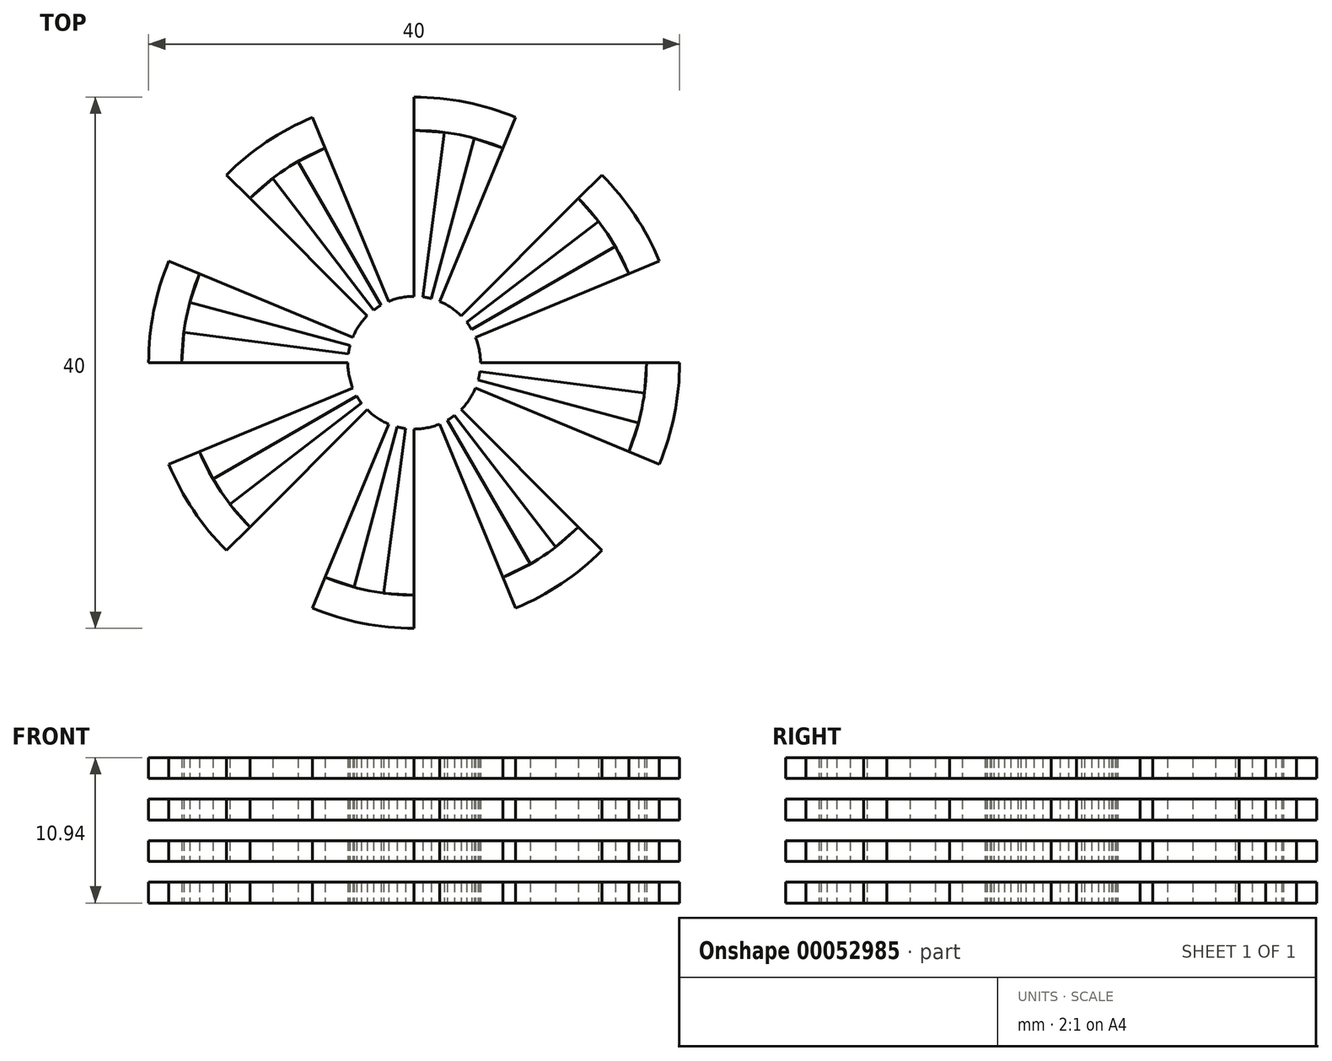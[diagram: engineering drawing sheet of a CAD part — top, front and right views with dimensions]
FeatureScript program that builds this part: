
annotation { "Feature Type Name" : "Feature", "Feature Type Description" : "" }
export const myFeature = defineFeature(function(context is Context, id is Id, definition is map)
    precondition{}
    {
        {
            var Q0;
            Q0=qCreatedBy(makeId("Top.planeOp"),FACE);
            var sketch = newSketch(context, id + "F0", { "sketchPlane" : qUnion([Q0])});
            skCircle(sketch, "E0", {"center": v(0, 0) * mm, "radius": 20 * mm});
            skCircle(sketch, "E1.cCircle", {"center": v(0, 0) * mm, "radius": 20 * mm, "construction": true});
            skLineSegment(sketch, "E1.0", {"start": v(0, -20) * mm, "end": v(-7.65, -18.48) * mm, "construction": true});
            skLineSegment(sketch, "E1.1", {"start": v(-7.65, -18.48) * mm, "end": v(-14.14, -14.14) * mm, "construction": true});
            skLineSegment(sketch, "E1.2", {"start": v(-14.14, -14.14) * mm, "end": v(-18.48, -7.65) * mm, "construction": true});
            skLineSegment(sketch, "E1.3", {"start": v(-18.48, -7.65) * mm, "end": v(-20, 0) * mm, "construction": true});
            skLineSegment(sketch, "E1.4", {"start": v(-20, 0) * mm, "end": v(-18.48, 7.65) * mm, "construction": true});
            skLineSegment(sketch, "E1.5", {"start": v(-18.48, 7.65) * mm, "end": v(-14.14, 14.14) * mm, "construction": true});
            skLineSegment(sketch, "E1.6", {"start": v(-14.14, 14.14) * mm, "end": v(-7.65, 18.48) * mm, "construction": true});
            skLineSegment(sketch, "E1.7", {"start": v(-7.65, 18.48) * mm, "end": v(0, 20) * mm, "construction": true});
            skLineSegment(sketch, "E1.8", {"start": v(0, 20) * mm, "end": v(7.65, 18.48) * mm, "construction": true});
            skLineSegment(sketch, "E1.9", {"start": v(7.65, 18.48) * mm, "end": v(14.14, 14.14) * mm, "construction": true});
            skLineSegment(sketch, "E1.10", {"start": v(14.14, 14.14) * mm, "end": v(18.48, 7.65) * mm, "construction": true});
            skLineSegment(sketch, "E1.11", {"start": v(18.48, 7.65) * mm, "end": v(20, 0) * mm, "construction": true});
            skLineSegment(sketch, "E1.12", {"start": v(20, 0) * mm, "end": v(18.48, -7.65) * mm, "construction": true});
            skLineSegment(sketch, "E1.13", {"start": v(18.48, -7.65) * mm, "end": v(14.14, -14.14) * mm, "construction": true});
            skLineSegment(sketch, "E1.14", {"start": v(14.14, -14.14) * mm, "end": v(7.65, -18.48) * mm, "construction": true});
            skLineSegment(sketch, "E1.15", {"start": v(7.65, -18.48) * mm, "end": v(0, -20) * mm, "construction": true});
            skLineSegment(sketch, "E2", {"start": v(0, 20) * mm, "end": v(0, -20) * mm});
            skLineSegment(sketch, "E3", {"start": v(7.65, -18.48) * mm, "end": v(-7.65, 18.48) * mm});
            skLineSegment(sketch, "E4", {"start": v(14.14, -14.14) * mm, "end": v(-14.14, 14.14) * mm});
            skLineSegment(sketch, "E5", {"start": v(18.48, -7.65) * mm, "end": v(-18.48, 7.65) * mm});
            skLineSegment(sketch, "E6", {"start": v(20, 0) * mm, "end": v(-20, 0) * mm});
            skLineSegment(sketch, "E7", {"start": v(18.48, 7.65) * mm, "end": v(-18.48, -7.65) * mm});
            skLineSegment(sketch, "E8", {"start": v(14.14, 14.14) * mm, "end": v(-14.14, -14.14) * mm});
            skLineSegment(sketch, "E9", {"start": v(7.65, 18.48) * mm, "end": v(-7.65, -18.48) * mm});
            skCircle(sketch, "E10", {"center": v(0, 0) * mm, "radius": 17.5 * mm});
            skSolve(sketch);
        }
        {
            var Q0;
            Q0 = qSketchRegion(id + "F0", true);
            extrude(context, id + "F1", {"entities" : qUnion([Q0]), "depth" : 12.5 * mm});
        }
        {
            var Q0;
            {var subQ0=sQuery(id+"F0.wireOp",EDGE,"E2");var subQ1=sQuery(id+"F0.wireOp",EDGE,"E0");var subQ2=makeQuery(id+"F0.imprint","INTERSECT",VERTEX,{"disambiguationData":[OD(0.0)],"derivedFrom":[subQ1,subQ0]});Q0=makeQuery(id+"F0.imprint","IMPRINT",FACE,{"disambiguationData":[TD([[makeQuery(id+"F0.imprint","IMPRINT",EDGE,{"disambiguationData":[TD([[subQ2,-1.0]])],"derivedFrom":subQ1}),1.0]])]});}
            var Q1;
            {var subQ0=sQuery(id+"F0.wireOp",EDGE,"E4");var subQ1=sQuery(id+"F0.wireOp",EDGE,"E0");var subQ2=makeQuery(id+"F0.imprint","INTERSECT",VERTEX,{"disambiguationData":[OD(1.0)],"derivedFrom":[subQ1,subQ0]});Q1=makeQuery(id+"F0.imprint","IMPRINT",FACE,{"disambiguationData":[TD([[makeQuery(id+"F0.imprint","IMPRINT",EDGE,{"disambiguationData":[TD([[subQ2,-1.0]])],"derivedFrom":subQ1}),1.0]])]});}
            var Q2;
            {var subQ0=sQuery(id+"F0.wireOp",EDGE,"E6");var subQ1=sQuery(id+"F0.wireOp",EDGE,"E0");var subQ2=makeQuery(id+"F0.imprint","INTERSECT",VERTEX,{"disambiguationData":[OD(1.0)],"derivedFrom":[subQ1,subQ0]});Q2=makeQuery(id+"F0.imprint","IMPRINT",FACE,{"disambiguationData":[TD([[makeQuery(id+"F0.imprint","IMPRINT",EDGE,{"disambiguationData":[TD([[subQ2,-1.0]])],"derivedFrom":subQ1}),1.0]])]});}
            var Q3;
            {var subQ0=sQuery(id+"F0.wireOp",EDGE,"E8");var subQ1=sQuery(id+"F0.wireOp",EDGE,"E0");var subQ2=makeQuery(id+"F0.imprint","INTERSECT",VERTEX,{"disambiguationData":[OD(1.0)],"derivedFrom":[subQ1,subQ0]});Q3=makeQuery(id+"F0.imprint","IMPRINT",FACE,{"disambiguationData":[TD([[makeQuery(id+"F0.imprint","IMPRINT",EDGE,{"disambiguationData":[TD([[subQ2,-1.0]])],"derivedFrom":subQ1}),1.0]])]});}
            var Q4;
            {var subQ0=sQuery(id+"F0.wireOp",EDGE,"E2");var subQ1=sQuery(id+"F0.wireOp",EDGE,"E0");var subQ2=makeQuery(id+"F0.imprint","INTERSECT",VERTEX,{"disambiguationData":[OD(1.0)],"derivedFrom":[subQ1,subQ0]});Q4=makeQuery(id+"F0.imprint","IMPRINT",FACE,{"disambiguationData":[TD([[makeQuery(id+"F0.imprint","IMPRINT",EDGE,{"disambiguationData":[TD([[subQ2,-1.0]])],"derivedFrom":subQ1}),1.0]])]});}
            var Q5;
            {var subQ0=sQuery(id+"F0.wireOp",EDGE,"E4");var subQ1=sQuery(id+"F0.wireOp",EDGE,"E0");var subQ2=makeQuery(id+"F0.imprint","INTERSECT",VERTEX,{"disambiguationData":[OD(0.0)],"derivedFrom":[subQ1,subQ0]});Q5=makeQuery(id+"F0.imprint","IMPRINT",FACE,{"disambiguationData":[TD([[makeQuery(id+"F0.imprint","IMPRINT",EDGE,{"disambiguationData":[TD([[subQ2,-1.0]])],"derivedFrom":subQ1}),1.0]])]});}
            var Q6;
            {var subQ0=sQuery(id+"F0.wireOp",EDGE,"E6");var subQ1=sQuery(id+"F0.wireOp",EDGE,"E0");var subQ2=makeQuery(id+"F0.imprint","INTERSECT",VERTEX,{"disambiguationData":[OD(0.0)],"derivedFrom":[subQ1,subQ0]});Q6=makeQuery(id+"F0.imprint","IMPRINT",FACE,{"disambiguationData":[TD([[makeQuery(id+"F0.imprint","IMPRINT",EDGE,{"disambiguationData":[TD([[subQ2,-1.0]])],"derivedFrom":subQ1}),1.0]])]});}
            var Q7;
            {var subQ0=sQuery(id+"F0.wireOp",EDGE,"E8");var subQ1=sQuery(id+"F0.wireOp",EDGE,"E0");var subQ2=makeQuery(id+"F0.imprint","INTERSECT",VERTEX,{"disambiguationData":[OD(0.0)],"derivedFrom":[subQ1,subQ0]});Q7=makeQuery(id+"F0.imprint","IMPRINT",FACE,{"disambiguationData":[TD([[makeQuery(id+"F0.imprint","IMPRINT",EDGE,{"disambiguationData":[TD([[subQ2,-1.0]])],"derivedFrom":subQ1}),1.0]])]});}
            extrude(context, id + "F2", {"entities" : qUnion([Q0, Q1, Q2, Q3, Q4, Q5, Q6, Q7]), "operationType" : NewBodyOperationType.REMOVE, "depth" : 12.5 * mm});
        }
        {
            var Q0;
            Q0=qCreatedBy(makeId("Top.planeOp"),FACE);
            var sketch = newSketch(context, id + "F3", { "sketchPlane" : qUnion([Q0])});
            skCircle(sketch, "E11.cCircle", {"center": v(0, 0) * mm, "radius": 17.5 * mm});
            skLineSegment(sketch, "E11.0", {"start": v(0, 17.5) * mm, "end": v(2.28, 17.35) * mm});
            skLineSegment(sketch, "E11.1", {"start": v(2.28, 17.35) * mm, "end": v(4.53, 16.9) * mm});
            skLineSegment(sketch, "E11.2", {"start": v(4.53, 16.9) * mm, "end": v(6.7, 16.17) * mm});
            skLineSegment(sketch, "E11.3", {"start": v(6.7, 16.17) * mm, "end": v(8.75, 15.16) * mm});
            skLineSegment(sketch, "E11.4", {"start": v(8.75, 15.16) * mm, "end": v(10.65, 13.88) * mm});
            skLineSegment(sketch, "E11.5", {"start": v(10.65, 13.88) * mm, "end": v(12.37, 12.37) * mm});
            skLineSegment(sketch, "E11.6", {"start": v(12.37, 12.37) * mm, "end": v(13.88, 10.65) * mm});
            skLineSegment(sketch, "E11.7", {"start": v(13.88, 10.65) * mm, "end": v(15.16, 8.75) * mm});
            skLineSegment(sketch, "E11.8", {"start": v(15.16, 8.75) * mm, "end": v(16.17, 6.7) * mm});
            skLineSegment(sketch, "E11.9", {"start": v(16.17, 6.7) * mm, "end": v(16.9, 4.53) * mm});
            skLineSegment(sketch, "E11.10", {"start": v(16.9, 4.53) * mm, "end": v(17.35, 2.28) * mm});
            skLineSegment(sketch, "E11.11", {"start": v(17.35, 2.28) * mm, "end": v(17.5, 0) * mm});
            skLineSegment(sketch, "E11.12", {"start": v(17.5, 0) * mm, "end": v(17.35, -2.28) * mm});
            skLineSegment(sketch, "E11.13", {"start": v(17.35, -2.28) * mm, "end": v(16.9, -4.53) * mm});
            skLineSegment(sketch, "E11.14", {"start": v(16.9, -4.53) * mm, "end": v(16.17, -6.7) * mm});
            skLineSegment(sketch, "E11.15", {"start": v(16.17, -6.7) * mm, "end": v(15.16, -8.75) * mm});
            skLineSegment(sketch, "E11.16", {"start": v(15.16, -8.75) * mm, "end": v(13.88, -10.65) * mm});
            skLineSegment(sketch, "E11.17", {"start": v(13.88, -10.65) * mm, "end": v(12.37, -12.37) * mm});
            skLineSegment(sketch, "E11.18", {"start": v(12.37, -12.37) * mm, "end": v(10.65, -13.88) * mm});
            skLineSegment(sketch, "E11.19", {"start": v(10.65, -13.88) * mm, "end": v(8.75, -15.16) * mm});
            skLineSegment(sketch, "E11.20", {"start": v(8.75, -15.16) * mm, "end": v(6.7, -16.17) * mm});
            skLineSegment(sketch, "E11.21", {"start": v(6.7, -16.17) * mm, "end": v(4.53, -16.9) * mm});
            skLineSegment(sketch, "E11.22", {"start": v(4.53, -16.9) * mm, "end": v(2.28, -17.35) * mm});
            skLineSegment(sketch, "E11.23", {"start": v(2.28, -17.35) * mm, "end": v(0, -17.5) * mm});
            skLineSegment(sketch, "E11.24", {"start": v(0, -17.5) * mm, "end": v(-2.28, -17.35) * mm});
            skLineSegment(sketch, "E11.25", {"start": v(-2.28, -17.35) * mm, "end": v(-4.53, -16.9) * mm});
            skLineSegment(sketch, "E11.26", {"start": v(-4.53, -16.9) * mm, "end": v(-6.7, -16.17) * mm});
            skLineSegment(sketch, "E11.27", {"start": v(-6.7, -16.17) * mm, "end": v(-8.75, -15.16) * mm});
            skLineSegment(sketch, "E11.28", {"start": v(-8.75, -15.16) * mm, "end": v(-10.65, -13.88) * mm});
            skLineSegment(sketch, "E11.29", {"start": v(-10.65, -13.88) * mm, "end": v(-12.37, -12.37) * mm});
            skLineSegment(sketch, "E11.30", {"start": v(-12.37, -12.37) * mm, "end": v(-13.88, -10.65) * mm});
            skLineSegment(sketch, "E11.31", {"start": v(-13.88, -10.65) * mm, "end": v(-15.16, -8.75) * mm});
            skLineSegment(sketch, "E11.32", {"start": v(-15.16, -8.75) * mm, "end": v(-16.17, -6.7) * mm});
            skLineSegment(sketch, "E11.33", {"start": v(-16.17, -6.7) * mm, "end": v(-16.9, -4.53) * mm});
            skLineSegment(sketch, "E11.34", {"start": v(-16.9, -4.53) * mm, "end": v(-17.35, -2.28) * mm});
            skLineSegment(sketch, "E11.35", {"start": v(-17.35, -2.28) * mm, "end": v(-17.5, 0) * mm});
            skLineSegment(sketch, "E11.36", {"start": v(-17.5, 0) * mm, "end": v(-17.35, 2.28) * mm});
            skLineSegment(sketch, "E11.37", {"start": v(-17.35, 2.28) * mm, "end": v(-16.9, 4.53) * mm});
            skLineSegment(sketch, "E11.38", {"start": v(-16.9, 4.53) * mm, "end": v(-16.17, 6.7) * mm});
            skLineSegment(sketch, "E11.39", {"start": v(-16.17, 6.7) * mm, "end": v(-15.16, 8.75) * mm});
            skLineSegment(sketch, "E11.40", {"start": v(-15.16, 8.75) * mm, "end": v(-13.88, 10.65) * mm});
            skLineSegment(sketch, "E11.41", {"start": v(-13.88, 10.65) * mm, "end": v(-12.37, 12.37) * mm});
            skLineSegment(sketch, "E11.42", {"start": v(-12.37, 12.37) * mm, "end": v(-10.65, 13.88) * mm});
            skLineSegment(sketch, "E11.43", {"start": v(-10.65, 13.88) * mm, "end": v(-8.75, 15.16) * mm});
            skLineSegment(sketch, "E11.44", {"start": v(-8.75, 15.16) * mm, "end": v(-6.7, 16.17) * mm});
            skLineSegment(sketch, "E11.45", {"start": v(-6.7, 16.17) * mm, "end": v(-4.53, 16.9) * mm});
            skLineSegment(sketch, "E11.46", {"start": v(-4.53, 16.9) * mm, "end": v(-2.28, 17.35) * mm});
            skLineSegment(sketch, "E11.47", {"start": v(-2.28, 17.35) * mm, "end": v(0, 17.5) * mm});
            skLineSegment(sketch, "E12", {"start": v(0, 17.5) * mm, "end": v(0, 0) * mm});
            skLineSegment(sketch, "E13", {"start": v(2.28, 17.35) * mm, "end": v(0, 0) * mm});
            skLineSegment(sketch, "E14", {"start": v(4.53, 16.9) * mm, "end": v(0, 0) * mm});
            skLineSegment(sketch, "E15", {"start": v(6.7, 16.17) * mm, "end": v(0, 0) * mm});
            skLineSegment(sketch, "E16", {"start": v(12.37, 12.37) * mm, "end": v(0, 0) * mm});
            skLineSegment(sketch, "E17", {"start": v(13.88, 10.65) * mm, "end": v(0, 0) * mm});
            skLineSegment(sketch, "E18", {"start": v(15.16, 8.75) * mm, "end": v(0, 0) * mm});
            skLineSegment(sketch, "E19", {"start": v(16.17, 6.7) * mm, "end": v(0, 0) * mm});
            skCircle(sketch, "E20", {"center": v(0, 0) * mm, "radius": 5 * mm});
            skLineSegment(sketch, "E21", {"start": v(17.5, 0) * mm, "end": v(0, 0) * mm});
            skLineSegment(sketch, "E22", {"start": v(17.35, -2.28) * mm, "end": v(0, 0) * mm});
            skLineSegment(sketch, "E23", {"start": v(16.9, -4.53) * mm, "end": v(0, 0) * mm});
            skLineSegment(sketch, "E24", {"start": v(16.17, -6.7) * mm, "end": v(0, 0) * mm});
            skLineSegment(sketch, "E25", {"start": v(12.37, -12.37) * mm, "end": v(0, 0) * mm});
            skLineSegment(sketch, "E26", {"start": v(10.65, -13.88) * mm, "end": v(0, 0) * mm});
            skLineSegment(sketch, "E27", {"start": v(8.75, -15.16) * mm, "end": v(0, 0) * mm});
            skLineSegment(sketch, "E28", {"start": v(6.7, -16.17) * mm, "end": v(0, 0) * mm});
            skLineSegment(sketch, "E29", {"start": v(0, 0) * mm, "end": v(0, -17.5) * mm});
            skLineSegment(sketch, "E30", {"start": v(0, 0) * mm, "end": v(-2.28, -17.35) * mm});
            skLineSegment(sketch, "E31", {"start": v(0, 0) * mm, "end": v(-4.53, -16.9) * mm});
            skLineSegment(sketch, "E32", {"start": v(0, 0) * mm, "end": v(-6.7, -16.17) * mm});
            skLineSegment(sketch, "E33", {"start": v(0, 0) * mm, "end": v(-12.37, -12.37) * mm});
            skLineSegment(sketch, "E34", {"start": v(0, 0) * mm, "end": v(-13.88, -10.65) * mm});
            skLineSegment(sketch, "E35", {"start": v(0, 0) * mm, "end": v(-15.16, -8.75) * mm});
            skLineSegment(sketch, "E36", {"start": v(0, 0) * mm, "end": v(-16.17, -6.7) * mm});
            skLineSegment(sketch, "E37", {"start": v(0, 0) * mm, "end": v(-17.5, 0) * mm});
            skLineSegment(sketch, "E38", {"start": v(0, 0) * mm, "end": v(-17.35, 2.28) * mm});
            skLineSegment(sketch, "E39", {"start": v(0, 0) * mm, "end": v(-16.9, 4.53) * mm});
            skLineSegment(sketch, "E40", {"start": v(0, 0) * mm, "end": v(-16.17, 6.7) * mm});
            skLineSegment(sketch, "E41", {"start": v(0, 0) * mm, "end": v(-12.37, 12.37) * mm});
            skLineSegment(sketch, "E42", {"start": v(0, 0) * mm, "end": v(-10.65, 13.88) * mm});
            skLineSegment(sketch, "E43", {"start": v(0, 0) * mm, "end": v(-8.75, 15.16) * mm});
            skLineSegment(sketch, "E44", {"start": v(0, 0) * mm, "end": v(-6.7, 16.17) * mm});
            skSolve(sketch);
        }
        {
            var Q0;
            {var subQ0=sQuery(id+"F3.wireOp",EDGE,"E31");var subQ1=sQuery(id+"F3.wireOp",EDGE,"E20");var subQ2=makeQuery(id+"F3.imprint","INTERSECT",VERTEX,{"derivedFrom":[subQ1,subQ0]});Q0=makeQuery(id+"F3.imprint","IMPRINT",FACE,{"disambiguationData":[TD([[makeQuery(id+"F3.imprint","IMPRINT",EDGE,{"disambiguationData":[TD([[subQ2,-1.0]])],"derivedFrom":subQ1}),1.0]])]});}
            var Q1;
            {var subQ1=sQuery(id+"F3.wireOp",EDGE,"E17");var subQ3=sQuery(id+"F3.wireOp",EDGE,"E20");var subQ4=makeQuery(id+"F3.imprint","INTERSECT",VERTEX,{"derivedFrom":[subQ1,subQ3]});Q1=makeQuery(id+"F3.imprint","IMPRINT",FACE,{"disambiguationData":[TD([[makeQuery(id+"F3.imprint","IMPRINT",EDGE,{"disambiguationData":[TD([[subQ4,1.0]])],"derivedFrom":subQ3}),1.0]])]});}
            var Q2;
            {var subQ0=sQuery(id+"F3.wireOp",EDGE,"E30");var subQ1=sQuery(id+"F3.wireOp",EDGE,"E20");var subQ2=makeQuery(id+"F3.imprint","INTERSECT",VERTEX,{"derivedFrom":[subQ1,subQ0]});Q2=makeQuery(id+"F3.imprint","IMPRINT",FACE,{"disambiguationData":[TD([[makeQuery(id+"F3.imprint","IMPRINT",EDGE,{"disambiguationData":[TD([[subQ2,-1.0]])],"derivedFrom":subQ1}),1.0]])]});}
            var Q3;
            {var subQ1=sQuery(id+"F3.wireOp",EDGE,"E18");var subQ3=sQuery(id+"F3.wireOp",EDGE,"E20");var subQ4=makeQuery(id+"F3.imprint","INTERSECT",VERTEX,{"derivedFrom":[subQ1,subQ3]});Q3=makeQuery(id+"F3.imprint","IMPRINT",FACE,{"disambiguationData":[TD([[makeQuery(id+"F3.imprint","IMPRINT",EDGE,{"disambiguationData":[TD([[subQ4,1.0]])],"derivedFrom":subQ3}),1.0]])]});}
            var Q4;
            {var subQ0=sQuery(id+"F3.wireOp",EDGE,"E29");var subQ1=sQuery(id+"F3.wireOp",EDGE,"E20");var subQ2=makeQuery(id+"F3.imprint","INTERSECT",VERTEX,{"derivedFrom":[subQ1,subQ0]});Q4=makeQuery(id+"F3.imprint","IMPRINT",FACE,{"disambiguationData":[TD([[makeQuery(id+"F3.imprint","IMPRINT",EDGE,{"disambiguationData":[TD([[subQ2,-1.0]])],"derivedFrom":subQ1}),1.0]])]});}
            var Q5;
            {var subQ1=sQuery(id+"F3.wireOp",EDGE,"E19");var subQ3=sQuery(id+"F3.wireOp",EDGE,"E20");var subQ4=makeQuery(id+"F3.imprint","INTERSECT",VERTEX,{"derivedFrom":[subQ1,subQ3]});Q5=makeQuery(id+"F3.imprint","IMPRINT",FACE,{"disambiguationData":[TD([[makeQuery(id+"F3.imprint","IMPRINT",EDGE,{"disambiguationData":[TD([[subQ4,1.0]])],"derivedFrom":subQ3}),1.0]])]});}
            var Q6;
            {var subQ0=sQuery(id+"F3.wireOp",EDGE,"E21");var subQ1=sQuery(id+"F3.wireOp",EDGE,"E20");var subQ2=makeQuery(id+"F3.imprint","INTERSECT",VERTEX,{"derivedFrom":[subQ1,subQ0]});Q6=makeQuery(id+"F3.imprint","IMPRINT",FACE,{"disambiguationData":[TD([[makeQuery(id+"F3.imprint","IMPRINT",EDGE,{"disambiguationData":[TD([[subQ2,1.0]])],"derivedFrom":subQ1}),1.0]])]});}
            var Q7;
            {var subQ0=sQuery(id+"F3.wireOp",EDGE,"E28");var subQ1=sQuery(id+"F3.wireOp",EDGE,"E20");var subQ2=makeQuery(id+"F3.imprint","INTERSECT",VERTEX,{"derivedFrom":[subQ1,subQ0]});Q7=makeQuery(id+"F3.imprint","IMPRINT",FACE,{"disambiguationData":[TD([[makeQuery(id+"F3.imprint","IMPRINT",EDGE,{"disambiguationData":[TD([[subQ2,-1.0]])],"derivedFrom":subQ1}),1.0]])]});}
            var Q8;
            {var subQ0=sQuery(id+"F3.wireOp",EDGE,"E44");var subQ1=sQuery(id+"F3.wireOp",EDGE,"E20");var subQ2=makeQuery(id+"F3.imprint","INTERSECT",VERTEX,{"derivedFrom":[subQ1,subQ0]});Q8=makeQuery(id+"F3.imprint","IMPRINT",FACE,{"disambiguationData":[TD([[makeQuery(id+"F3.imprint","IMPRINT",EDGE,{"disambiguationData":[TD([[subQ2,-1.0]])],"derivedFrom":subQ1}),1.0]])]});}
            var Q9;
            {var subQ0=sQuery(id+"F3.wireOp",EDGE,"E27");var subQ1=sQuery(id+"F3.wireOp",EDGE,"E20");var subQ2=makeQuery(id+"F3.imprint","INTERSECT",VERTEX,{"derivedFrom":[subQ1,subQ0]});Q9=makeQuery(id+"F3.imprint","IMPRINT",FACE,{"disambiguationData":[TD([[makeQuery(id+"F3.imprint","IMPRINT",EDGE,{"disambiguationData":[TD([[subQ2,-1.0]])],"derivedFrom":subQ1}),1.0]])]});}
            var Q10;
            {var subQ0=sQuery(id+"F3.wireOp",EDGE,"E43");var subQ1=sQuery(id+"F3.wireOp",EDGE,"E20");var subQ2=makeQuery(id+"F3.imprint","INTERSECT",VERTEX,{"derivedFrom":[subQ1,subQ0]});Q10=makeQuery(id+"F3.imprint","IMPRINT",FACE,{"disambiguationData":[TD([[makeQuery(id+"F3.imprint","IMPRINT",EDGE,{"disambiguationData":[TD([[subQ2,-1.0]])],"derivedFrom":subQ1}),1.0]])]});}
            var Q11;
            {var subQ0=sQuery(id+"F3.wireOp",EDGE,"E40");var subQ1=sQuery(id+"F3.wireOp",EDGE,"E20");var subQ2=makeQuery(id+"F3.imprint","INTERSECT",VERTEX,{"derivedFrom":[subQ1,subQ0]});Q11=makeQuery(id+"F3.imprint","IMPRINT",FACE,{"disambiguationData":[TD([[makeQuery(id+"F3.imprint","IMPRINT",EDGE,{"disambiguationData":[TD([[subQ2,-1.0]])],"derivedFrom":subQ1}),1.0]])]});}
            var Q12;
            {var subQ0=sQuery(id+"F3.wireOp",EDGE,"E24");var subQ1=sQuery(id+"F3.wireOp",EDGE,"E20");var subQ2=makeQuery(id+"F3.imprint","INTERSECT",VERTEX,{"derivedFrom":[subQ1,subQ0]});Q12=makeQuery(id+"F3.imprint","IMPRINT",FACE,{"disambiguationData":[TD([[makeQuery(id+"F3.imprint","IMPRINT",EDGE,{"disambiguationData":[TD([[subQ2,-1.0]])],"derivedFrom":subQ1}),1.0]])]});}
            var Q13;
            {var subQ0=sQuery(id+"F3.wireOp",EDGE,"E26");var subQ1=sQuery(id+"F3.wireOp",EDGE,"E20");var subQ2=makeQuery(id+"F3.imprint","INTERSECT",VERTEX,{"derivedFrom":[subQ1,subQ0]});Q13=makeQuery(id+"F3.imprint","IMPRINT",FACE,{"disambiguationData":[TD([[makeQuery(id+"F3.imprint","IMPRINT",EDGE,{"disambiguationData":[TD([[subQ2,-1.0]])],"derivedFrom":subQ1}),1.0]])]});}
            var Q14;
            {var subQ0=sQuery(id+"F3.wireOp",EDGE,"E42");var subQ1=sQuery(id+"F3.wireOp",EDGE,"E20");var subQ2=makeQuery(id+"F3.imprint","INTERSECT",VERTEX,{"derivedFrom":[subQ1,subQ0]});Q14=makeQuery(id+"F3.imprint","IMPRINT",FACE,{"disambiguationData":[TD([[makeQuery(id+"F3.imprint","IMPRINT",EDGE,{"disambiguationData":[TD([[subQ2,-1.0]])],"derivedFrom":subQ1}),1.0]])]});}
            var Q15;
            {var subQ0=sQuery(id+"F3.wireOp",EDGE,"E23");var subQ1=sQuery(id+"F3.wireOp",EDGE,"E20");var subQ2=makeQuery(id+"F3.imprint","INTERSECT",VERTEX,{"derivedFrom":[subQ1,subQ0]});Q15=makeQuery(id+"F3.imprint","IMPRINT",FACE,{"disambiguationData":[TD([[makeQuery(id+"F3.imprint","IMPRINT",EDGE,{"disambiguationData":[TD([[subQ2,-1.0]])],"derivedFrom":subQ1}),1.0]])]});}
            var Q16;
            {var subQ0=sQuery(id+"F3.wireOp",EDGE,"E25");var subQ1=sQuery(id+"F3.wireOp",EDGE,"E20");var subQ2=makeQuery(id+"F3.imprint","INTERSECT",VERTEX,{"derivedFrom":[subQ1,subQ0]});Q16=makeQuery(id+"F3.imprint","IMPRINT",FACE,{"disambiguationData":[TD([[makeQuery(id+"F3.imprint","IMPRINT",EDGE,{"disambiguationData":[TD([[subQ2,-1.0]])],"derivedFrom":subQ1}),1.0]])]});}
            var Q17;
            {var subQ0=sQuery(id+"F3.wireOp",EDGE,"E41");var subQ1=sQuery(id+"F3.wireOp",EDGE,"E20");var subQ2=makeQuery(id+"F3.imprint","INTERSECT",VERTEX,{"derivedFrom":[subQ1,subQ0]});Q17=makeQuery(id+"F3.imprint","IMPRINT",FACE,{"disambiguationData":[TD([[makeQuery(id+"F3.imprint","IMPRINT",EDGE,{"disambiguationData":[TD([[subQ2,-1.0]])],"derivedFrom":subQ1}),1.0]])]});}
            var Q18;
            {var subQ1=sQuery(id+"F3.wireOp",EDGE,"E12");var subQ3=sQuery(id+"F3.wireOp",EDGE,"E20");var subQ4=makeQuery(id+"F3.imprint","INTERSECT",VERTEX,{"derivedFrom":[subQ1,subQ3]});Q18=makeQuery(id+"F3.imprint","IMPRINT",FACE,{"disambiguationData":[TD([[makeQuery(id+"F3.imprint","IMPRINT",EDGE,{"disambiguationData":[TD([[subQ4,1.0]])],"derivedFrom":subQ3}),1.0]])]});}
            var Q19;
            {var subQ0=sQuery(id+"F3.wireOp",EDGE,"E36");var subQ1=sQuery(id+"F3.wireOp",EDGE,"E20");var subQ2=makeQuery(id+"F3.imprint","INTERSECT",VERTEX,{"derivedFrom":[subQ1,subQ0]});Q19=makeQuery(id+"F3.imprint","IMPRINT",FACE,{"disambiguationData":[TD([[makeQuery(id+"F3.imprint","IMPRINT",EDGE,{"disambiguationData":[TD([[subQ2,-1.0]])],"derivedFrom":subQ1}),1.0]])]});}
            var Q20;
            {var subQ1=sQuery(id+"F3.wireOp",EDGE,"E12");var subQ3=sQuery(id+"F3.wireOp",EDGE,"E20");var subQ4=makeQuery(id+"F3.imprint","INTERSECT",VERTEX,{"derivedFrom":[subQ1,subQ3]});Q20=makeQuery(id+"F3.imprint","IMPRINT",FACE,{"disambiguationData":[TD([[makeQuery(id+"F3.imprint","IMPRINT",EDGE,{"disambiguationData":[TD([[subQ4,-1.0]])],"derivedFrom":subQ3}),1.0]])]});}
            var Q21;
            {var subQ0=sQuery(id+"F3.wireOp",EDGE,"E35");var subQ1=sQuery(id+"F3.wireOp",EDGE,"E20");var subQ2=makeQuery(id+"F3.imprint","INTERSECT",VERTEX,{"derivedFrom":[subQ1,subQ0]});Q21=makeQuery(id+"F3.imprint","IMPRINT",FACE,{"disambiguationData":[TD([[makeQuery(id+"F3.imprint","IMPRINT",EDGE,{"disambiguationData":[TD([[subQ2,-1.0]])],"derivedFrom":subQ1}),1.0]])]});}
            var Q22;
            {var subQ1=sQuery(id+"F3.wireOp",EDGE,"E13");var subQ3=sQuery(id+"F3.wireOp",EDGE,"E20");var subQ4=makeQuery(id+"F3.imprint","INTERSECT",VERTEX,{"derivedFrom":[subQ1,subQ3]});Q22=makeQuery(id+"F3.imprint","IMPRINT",FACE,{"disambiguationData":[TD([[makeQuery(id+"F3.imprint","IMPRINT",EDGE,{"disambiguationData":[TD([[subQ4,1.0]])],"derivedFrom":subQ3}),1.0]])]});}
            var Q23;
            {var subQ0=sQuery(id+"F3.wireOp",EDGE,"E34");var subQ1=sQuery(id+"F3.wireOp",EDGE,"E20");var subQ2=makeQuery(id+"F3.imprint","INTERSECT",VERTEX,{"derivedFrom":[subQ1,subQ0]});Q23=makeQuery(id+"F3.imprint","IMPRINT",FACE,{"disambiguationData":[TD([[makeQuery(id+"F3.imprint","IMPRINT",EDGE,{"disambiguationData":[TD([[subQ2,-1.0]])],"derivedFrom":subQ1}),1.0]])]});}
            var Q24;
            {var subQ1=sQuery(id+"F3.wireOp",EDGE,"E14");var subQ3=sQuery(id+"F3.wireOp",EDGE,"E20");var subQ4=makeQuery(id+"F3.imprint","INTERSECT",VERTEX,{"derivedFrom":[subQ1,subQ3]});Q24=makeQuery(id+"F3.imprint","IMPRINT",FACE,{"disambiguationData":[TD([[makeQuery(id+"F3.imprint","IMPRINT",EDGE,{"disambiguationData":[TD([[subQ4,1.0]])],"derivedFrom":subQ3}),1.0]])]});}
            var Q25;
            {var subQ0=sQuery(id+"F3.wireOp",EDGE,"E33");var subQ1=sQuery(id+"F3.wireOp",EDGE,"E20");var subQ2=makeQuery(id+"F3.imprint","INTERSECT",VERTEX,{"derivedFrom":[subQ1,subQ0]});Q25=makeQuery(id+"F3.imprint","IMPRINT",FACE,{"disambiguationData":[TD([[makeQuery(id+"F3.imprint","IMPRINT",EDGE,{"disambiguationData":[TD([[subQ2,-1.0]])],"derivedFrom":subQ1}),1.0]])]});}
            var Q26;
            {var subQ1=sQuery(id+"F3.wireOp",EDGE,"E15");var subQ3=sQuery(id+"F3.wireOp",EDGE,"E20");var subQ4=makeQuery(id+"F3.imprint","INTERSECT",VERTEX,{"derivedFrom":[subQ1,subQ3]});Q26=makeQuery(id+"F3.imprint","IMPRINT",FACE,{"disambiguationData":[TD([[makeQuery(id+"F3.imprint","IMPRINT",EDGE,{"disambiguationData":[TD([[subQ4,1.0]])],"derivedFrom":subQ3}),1.0]])]});}
            var Q27;
            {var subQ0=sQuery(id+"F3.wireOp",EDGE,"E32");var subQ1=sQuery(id+"F3.wireOp",EDGE,"E20");var subQ2=makeQuery(id+"F3.imprint","INTERSECT",VERTEX,{"derivedFrom":[subQ1,subQ0]});Q27=makeQuery(id+"F3.imprint","IMPRINT",FACE,{"disambiguationData":[TD([[makeQuery(id+"F3.imprint","IMPRINT",EDGE,{"disambiguationData":[TD([[subQ2,-1.0]])],"derivedFrom":subQ1}),1.0]])]});}
            var Q28;
            {var subQ1=sQuery(id+"F3.wireOp",EDGE,"E16");var subQ3=sQuery(id+"F3.wireOp",EDGE,"E20");var subQ4=makeQuery(id+"F3.imprint","INTERSECT",VERTEX,{"derivedFrom":[subQ1,subQ3]});Q28=makeQuery(id+"F3.imprint","IMPRINT",FACE,{"disambiguationData":[TD([[makeQuery(id+"F3.imprint","IMPRINT",EDGE,{"disambiguationData":[TD([[subQ4,1.0]])],"derivedFrom":subQ3}),1.0]])]});}
            var Q29;
            {var subQ0=sQuery(id+"F3.wireOp",EDGE,"E38");var subQ1=sQuery(id+"F3.wireOp",EDGE,"E20");var subQ2=makeQuery(id+"F3.imprint","INTERSECT",VERTEX,{"derivedFrom":[subQ1,subQ0]});Q29=makeQuery(id+"F3.imprint","IMPRINT",FACE,{"disambiguationData":[TD([[makeQuery(id+"F3.imprint","IMPRINT",EDGE,{"disambiguationData":[TD([[subQ2,-1.0]])],"derivedFrom":subQ1}),1.0]])]});}
            var Q30;
            {var subQ0=sQuery(id+"F3.wireOp",EDGE,"E39");var subQ1=sQuery(id+"F3.wireOp",EDGE,"E20");var subQ2=makeQuery(id+"F3.imprint","INTERSECT",VERTEX,{"derivedFrom":[subQ1,subQ0]});Q30=makeQuery(id+"F3.imprint","IMPRINT",FACE,{"disambiguationData":[TD([[makeQuery(id+"F3.imprint","IMPRINT",EDGE,{"disambiguationData":[TD([[subQ2,-1.0]])],"derivedFrom":subQ1}),1.0]])]});}
            var Q31;
            {var subQ0=sQuery(id+"F3.wireOp",EDGE,"E37");var subQ1=sQuery(id+"F3.wireOp",EDGE,"E20");var subQ2=makeQuery(id+"F3.imprint","INTERSECT",VERTEX,{"derivedFrom":[subQ1,subQ0]});Q31=makeQuery(id+"F3.imprint","IMPRINT",FACE,{"disambiguationData":[TD([[makeQuery(id+"F3.imprint","IMPRINT",EDGE,{"disambiguationData":[TD([[subQ2,-1.0]])],"derivedFrom":subQ1}),1.0]])]});}
            var Q32;
            {var subQ0=sQuery(id+"F3.wireOp",EDGE,"E11.6");Q32=makeQuery(id+"F3.imprint","IMPRINT",FACE,{"disambiguationData":[TD([[makeQuery(id+"F3.imprint","IMPRINT",EDGE,{"derivedFrom":subQ0}),-1.0]])]});}
            var Q33;
            {var subQ0=sQuery(id+"F3.wireOp",EDGE,"E11.8");Q33=makeQuery(id+"F3.imprint","IMPRINT",FACE,{"disambiguationData":[TD([[makeQuery(id+"F3.imprint","IMPRINT",EDGE,{"derivedFrom":subQ0}),-1.0]])]});}
            var Q34;
            {var subQ0=sQuery(id+"F3.wireOp",EDGE,"E11.2");Q34=makeQuery(id+"F3.imprint","IMPRINT",FACE,{"disambiguationData":[TD([[makeQuery(id+"F3.imprint","IMPRINT",EDGE,{"derivedFrom":subQ0}),-1.0]])]});}
            var Q35;
            {var subQ0=sQuery(id+"F3.wireOp",EDGE,"E11.0");Q35=makeQuery(id+"F3.imprint","IMPRINT",FACE,{"disambiguationData":[TD([[makeQuery(id+"F3.imprint","IMPRINT",EDGE,{"derivedFrom":subQ0}),-1.0]])]});}
            var Q36;
            {var subQ0=sQuery(id+"F3.wireOp",EDGE,"E11.44");Q36=makeQuery(id+"F3.imprint","IMPRINT",FACE,{"disambiguationData":[TD([[makeQuery(id+"F3.imprint","IMPRINT",EDGE,{"derivedFrom":subQ0}),-1.0]])]});}
            var Q37;
            {var subQ0=sQuery(id+"F3.wireOp",EDGE,"E11.42");Q37=makeQuery(id+"F3.imprint","IMPRINT",FACE,{"disambiguationData":[TD([[makeQuery(id+"F3.imprint","IMPRINT",EDGE,{"derivedFrom":subQ0}),-1.0]])]});}
            var Q38;
            {var subQ0=sQuery(id+"F3.wireOp",EDGE,"E11.38");Q38=makeQuery(id+"F3.imprint","IMPRINT",FACE,{"disambiguationData":[TD([[makeQuery(id+"F3.imprint","IMPRINT",EDGE,{"derivedFrom":subQ0}),-1.0]])]});}
            var Q39;
            {var subQ0=sQuery(id+"F3.wireOp",EDGE,"E11.36");Q39=makeQuery(id+"F3.imprint","IMPRINT",FACE,{"disambiguationData":[TD([[makeQuery(id+"F3.imprint","IMPRINT",EDGE,{"derivedFrom":subQ0}),-1.0]])]});}
            var Q40;
            {var subQ0=sQuery(id+"F3.wireOp",EDGE,"E11.32");Q40=makeQuery(id+"F3.imprint","IMPRINT",FACE,{"disambiguationData":[TD([[makeQuery(id+"F3.imprint","IMPRINT",EDGE,{"derivedFrom":subQ0}),-1.0]])]});}
            var Q41;
            {var subQ0=sQuery(id+"F3.wireOp",EDGE,"E11.30");Q41=makeQuery(id+"F3.imprint","IMPRINT",FACE,{"disambiguationData":[TD([[makeQuery(id+"F3.imprint","IMPRINT",EDGE,{"derivedFrom":subQ0}),-1.0]])]});}
            var Q42;
            {var subQ0=sQuery(id+"F3.wireOp",EDGE,"E11.26");Q42=makeQuery(id+"F3.imprint","IMPRINT",FACE,{"disambiguationData":[TD([[makeQuery(id+"F3.imprint","IMPRINT",EDGE,{"derivedFrom":subQ0}),-1.0]])]});}
            var Q43;
            {var subQ0=sQuery(id+"F3.wireOp",EDGE,"E11.24");Q43=makeQuery(id+"F3.imprint","IMPRINT",FACE,{"disambiguationData":[TD([[makeQuery(id+"F3.imprint","IMPRINT",EDGE,{"derivedFrom":subQ0}),-1.0]])]});}
            var Q44;
            {var subQ0=sQuery(id+"F3.wireOp",EDGE,"E11.20");Q44=makeQuery(id+"F3.imprint","IMPRINT",FACE,{"disambiguationData":[TD([[makeQuery(id+"F3.imprint","IMPRINT",EDGE,{"derivedFrom":subQ0}),-1.0]])]});}
            var Q45;
            {var subQ0=sQuery(id+"F3.wireOp",EDGE,"E11.18");Q45=makeQuery(id+"F3.imprint","IMPRINT",FACE,{"disambiguationData":[TD([[makeQuery(id+"F3.imprint","IMPRINT",EDGE,{"derivedFrom":subQ0}),-1.0]])]});}
            var Q46;
            {var subQ0=sQuery(id+"F3.wireOp",EDGE,"E11.14");Q46=makeQuery(id+"F3.imprint","IMPRINT",FACE,{"disambiguationData":[TD([[makeQuery(id+"F3.imprint","IMPRINT",EDGE,{"derivedFrom":subQ0}),-1.0]])]});}
            var Q47;
            {var subQ0=sQuery(id+"F3.wireOp",EDGE,"E11.12");Q47=makeQuery(id+"F3.imprint","IMPRINT",FACE,{"disambiguationData":[TD([[makeQuery(id+"F3.imprint","IMPRINT",EDGE,{"derivedFrom":subQ0}),-1.0]])]});}
            extrude(context, id + "F4", {"entities" : qUnion([Q0, Q1, Q2, Q3, Q4, Q5, Q6, Q7, Q8, Q9, Q10, Q11, Q12, Q13, Q14, Q15, Q16, Q17, Q18, Q19, Q20, Q21, Q22, Q23, Q24, Q25, Q26, Q27, Q28, Q29, Q30, Q31, Q32, Q33, Q34, Q35, Q36, Q37, Q38, Q39, Q40, Q41, Q42, Q43, Q44, Q45, Q46, Q47]), "depth" : 12.5 * mm});
        }
        {
            var Q0;
            Q0=qCreatedBy(makeId("Front.planeOp"),FACE);
            var sketch = newSketch(context, id + "F5", { "sketchPlane" : qUnion([Q0])});
            skLineSegment(sketch, "E45", {"start": v(0, 0) * mm, "end": v(0, 3.12) * mm});
            skLineSegment(sketch, "E46", {"start": v(0, 3.12) * mm, "end": v(0, 6.25) * mm});
            skLineSegment(sketch, "E47", {"start": v(0, 6.25) * mm, "end": v(0, 9.38) * mm});
            skLineSegment(sketch, "E48", {"start": v(0, 9.38) * mm, "end": v(0, 12.5) * mm});
            skPoint(sketch, "E49.oppositeSnap0", {"position": v(0, 10.94) * mm});
            skLineSegment(sketch, "E49.bottom", {"start": v(0, 9.38) * mm, "end": v(-20, 9.38) * mm});
            skLineSegment(sketch, "E49.top", {"start": v(0, 10.94) * mm, "end": v(-20, 10.94) * mm});
            skLineSegment(sketch, "E49.left", {"start": v(0, 9.38) * mm, "end": v(0, 10.94) * mm});
            skLineSegment(sketch, "E49.right", {"start": v(-20, 9.38) * mm, "end": v(-20, 10.94) * mm});
            skLineSegment(sketch, "E50.bottom", {"start": v(0, 7.81) * mm, "end": v(-20, 7.81) * mm});
            skLineSegment(sketch, "E50.top", {"start": v(0, 6.25) * mm, "end": v(-20, 6.25) * mm});
            skLineSegment(sketch, "E50.left", {"start": v(0, 7.81) * mm, "end": v(0, 6.25) * mm});
            skLineSegment(sketch, "E50.right", {"start": v(-20, 7.81) * mm, "end": v(-20, 6.25) * mm});
            skLineSegment(sketch, "E51.bottom", {"start": v(0, 4.69) * mm, "end": v(-20, 4.69) * mm});
            skLineSegment(sketch, "E51.top", {"start": v(0, 3.12) * mm, "end": v(-20, 3.12) * mm});
            skLineSegment(sketch, "E51.left", {"start": v(0, 4.69) * mm, "end": v(0, 3.12) * mm});
            skLineSegment(sketch, "E51.right", {"start": v(-20, 4.69) * mm, "end": v(-20, 3.13) * mm});
            skLineSegment(sketch, "E52.bottom", {"start": v(0, 1.56) * mm, "end": v(-20, 1.56) * mm});
            skLineSegment(sketch, "E52.top", {"start": v(0, 0) * mm, "end": v(-20, 0) * mm});
            skLineSegment(sketch, "E52.left", {"start": v(0, 1.56) * mm, "end": v(0, 0) * mm});
            skLineSegment(sketch, "E52.right", {"start": v(-20, 1.56) * mm, "end": v(-20, 0) * mm});
            skSolve(sketch);
        }
        {
            var Q0;
            Q0 = qSketchRegion(id + "F5", true);
            var Q1;
            Q1=sQuery(id+"F5.wireOp",EDGE,"E48");
            revolve(context, id + "F6", {"operationType" : NewBodyOperationType.REMOVE, "entities" : qUnion([Q0]), "axis" : qUnion([Q1]), "revolveType" : RevolveType.FULL, "oppositeDirection" : true});
        }
    });
